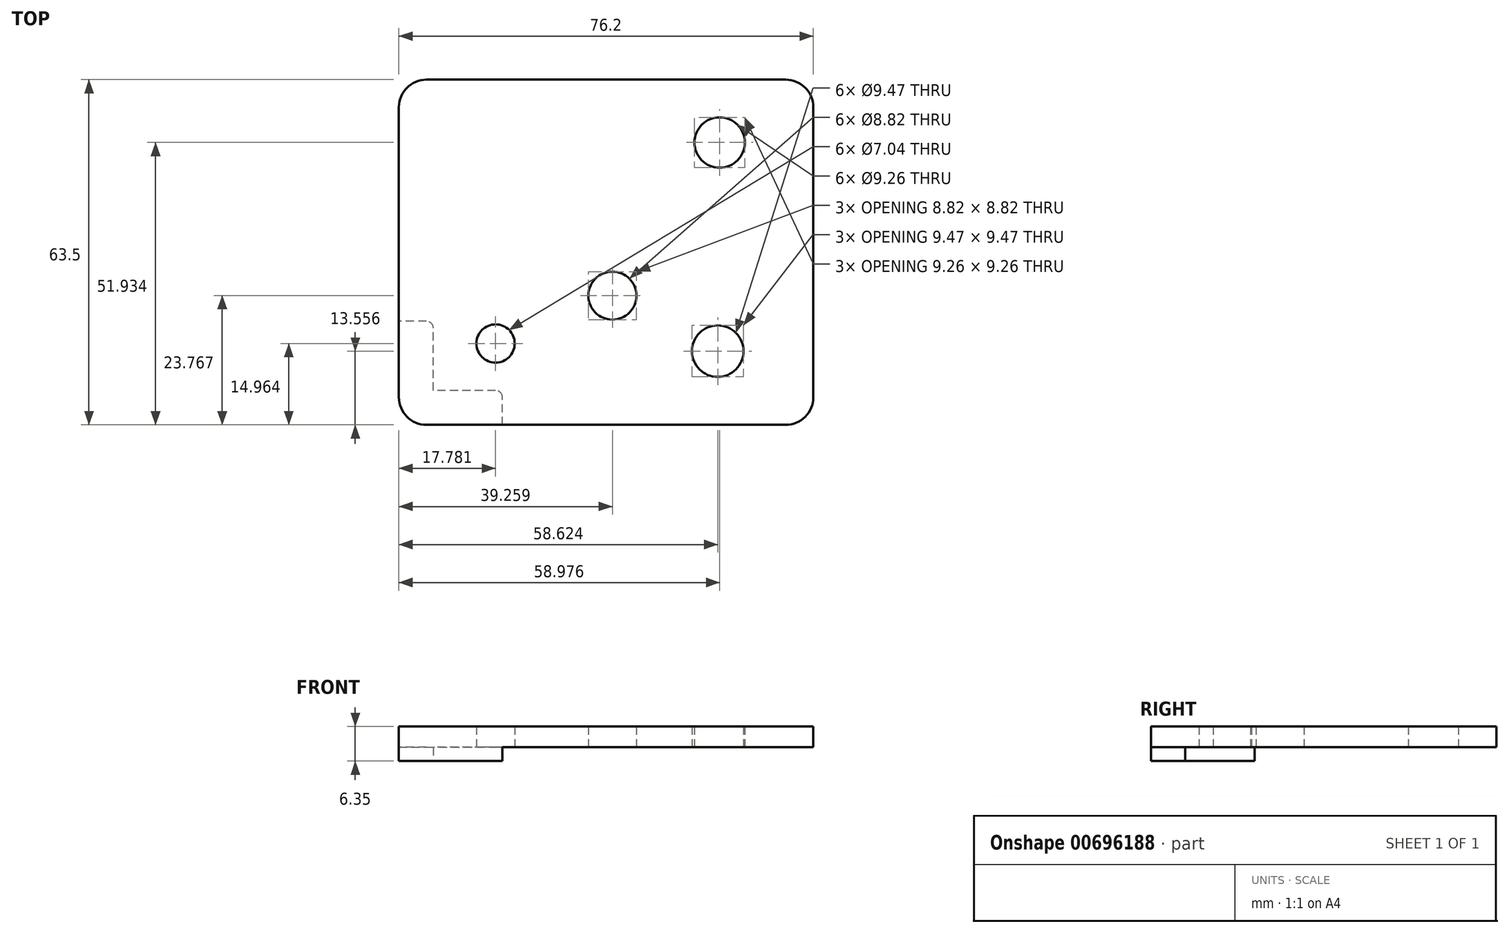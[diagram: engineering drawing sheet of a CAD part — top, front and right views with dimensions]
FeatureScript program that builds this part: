
annotation { "Feature Type Name" : "Feature", "Feature Type Description" : "" }
export const myFeature = defineFeature(function(context is Context, id is Id, definition is map)
    precondition{}
    {
        {
            var Q0;
            Q0=qCreatedBy(makeId("Top.planeOp"),FACE);
            var sketch = newSketch(context, id + "F0", { "sketchPlane" : qUnion([Q0])});
            skLineSegment(sketch, "E0.bottom", {"start": v(0, 0) * mm, "end": v(76.2, 0) * mm});
            skLineSegment(sketch, "E0.top", {"start": v(0, 63.5) * mm, "end": v(76.2, 63.5) * mm});
            skLineSegment(sketch, "E0.left", {"start": v(0, 0) * mm, "end": v(0, 63.5) * mm});
            skLineSegment(sketch, "E0.right", {"start": v(76.2, 0) * mm, "end": v(76.2, 63.5) * mm});
            skCircle(sketch, "E1", {"center": v(17.78, 14.96) * mm, "radius": 3.52 * mm});
            skCircle(sketch, "E2", {"center": v(39.26, 23.77) * mm, "radius": 4.41 * mm});
            skCircle(sketch, "E3", {"center": v(58.62, 13.56) * mm, "radius": 4.74 * mm});
            skCircle(sketch, "E4", {"center": v(58.98, 51.93) * mm, "radius": 4.63 * mm});
            skSolve(sketch);
        }
        {
            var Q0;
            Q0 = qSketchRegion(id + "F0", true);
            extrude(context, id + "F1", {"entities" : qUnion([Q0]), "depth" : 6.35 * mm, "offsetDistance" : 25.4 * mm});
        }
        {
            var Q0;
            Q0=makeQuery(id+"F1.opExtrude","CAP_FACE",FACE,{"disambiguationData":[OSD([sQuery(id+"F0.wireOp",EDGE,"E0.bottom"),sQuery(id+"F0.wireOp",EDGE,"E0.top"),sQuery(id+"F0.wireOp",EDGE,"E0.left"),sQuery(id+"F0.wireOp",EDGE,"E0.right"),sQuery(id+"F0.wireOp",EDGE,"E1"),sQuery(id+"F0.wireOp",EDGE,"E2"),sQuery(id+"F0.wireOp",EDGE,"E3"),sQuery(id+"F0.wireOp",EDGE,"E4")])],"isStart":true});
            var sketch = newSketch(context, id + "F2", { "sketchPlane" : qUnion([Q0])});
            skLineSegment(sketch, "E5", {"start": v(6.35, -6.32) * mm, "end": v(6.35, -19.05) * mm});
            skLineSegment(sketch, "E6", {"start": v(6.35, -19.05) * mm, "end": v(0, -19.05) * mm});
            skLineSegment(sketch, "E7", {"start": v(19.05, 0) * mm, "end": v(19.05, -6.32) * mm});
            skLineSegment(sketch, "E8", {"start": v(19.05, -6.32) * mm, "end": v(6.35, -6.32) * mm});
            skLineSegment(sketch, "E9", {"start": v(19.05, 0) * mm, "end": v(76.2, 0) * mm});
            skLineSegment(sketch, "E10", {"start": v(76.2, 0) * mm, "end": v(76.2, -63.5) * mm});
            skLineSegment(sketch, "E11", {"start": v(76.2, -63.5) * mm, "end": v(0, -63.5) * mm});
            skLineSegment(sketch, "E12", {"start": v(0, -63.5) * mm, "end": v(0, -19.05) * mm});
            skSolve(sketch);
        }
        {
            var Q0;
            Q0 = qSketchRegion(id + "F2", true);
            extrude(context, id + "F3", {"entities" : qUnion([Q0]), "operationType" : NewBodyOperationType.REMOVE, "oppositeDirection" : true, "depth" : 2.54 * mm, "offsetDistance" : 25.4 * mm});
        }
        {
            var Q0;
            Q0=makeQuery(id+"F1.opExtrude","SWEPT_EDGE",EDGE,{"disambiguationData":[OSD([sQuery(id+"F0.wireOp",EDGE,"E0.top"),sQuery(id+"F0.wireOp",EDGE,"E0.left")])]});
            var Q1;
            Q1=makeQuery(id+"F1.opExtrude","SWEPT_EDGE",EDGE,{"disambiguationData":[OSD([sQuery(id+"F0.wireOp",EDGE,"E0.top"),sQuery(id+"F0.wireOp",EDGE,"E0.right")])]});
            var Q2;
            Q2=makeQuery(id+"F1.opExtrude","SWEPT_EDGE",EDGE,{"disambiguationData":[OSD([sQuery(id+"F0.wireOp",EDGE,"E0.bottom"),sQuery(id+"F0.wireOp",EDGE,"E0.right")])]});
            var Q3;
            Q3=makeQuery(id+"F1.opExtrude","SWEPT_EDGE",EDGE,{"disambiguationData":[OSD([sQuery(id+"F0.wireOp",EDGE,"E0.bottom"),sQuery(id+"F0.wireOp",EDGE,"E0.left")])]});
            fillet(context, id + "F4", {"entities" : qUnion([Q0, Q1, Q2, Q3]), "radius" : 5.08 * mm, "tangentPropagation" : true, "allowEdgeOverflow" : false});
        }
        {
            var Q0;
            Q0=makeQuery(id+"F3.boolean.opBoolean","COPY",EDGE,{"derivedFrom":makeQuery(id+"F3.opExtrude","SWEPT_EDGE",EDGE,{"disambiguationData":[OSD([sQuery(id+"F2.wireOp",EDGE,"E5"),sQuery(id+"F2.wireOp",EDGE,"E6")])]})});
            var Q1;
            Q1=makeQuery(id+"F3.boolean.opBoolean","COPY",EDGE,{"derivedFrom":makeQuery(id+"F3.opExtrude","SWEPT_EDGE",EDGE,{"disambiguationData":[OSD([sQuery(id+"F2.wireOp",EDGE,"E7"),sQuery(id+"F2.wireOp",EDGE,"E8")])]})});
            var Q2;
            Q2=makeQuery(id+"F3.boolean.opBoolean","COPY",EDGE,{"derivedFrom":makeQuery(id+"F3.opExtrude","SWEPT_EDGE",EDGE,{"disambiguationData":[OSD([sQuery(id+"F0.wireOp",EDGE,"E0.left"),sQuery(id+"F2.wireOp",EDGE,"E6"),sQuery(id+"F2.wireOp",EDGE,"E12")])]})});
            var Q3;
            Q3=makeQuery(id+"F3.boolean.opBoolean","COPY",EDGE,{"derivedFrom":makeQuery(id+"F3.opExtrude","SWEPT_EDGE",EDGE,{"disambiguationData":[OSD([sQuery(id+"F0.wireOp",EDGE,"E0.bottom"),sQuery(id+"F2.wireOp",EDGE,"E7"),sQuery(id+"F2.wireOp",EDGE,"E9")])]})});
            fillet(context, id + "F5", {"entities" : qUnion([Q0, Q1, Q2, Q3]), "radius" : 1.27 * mm, "tangentPropagation" : true, "allowEdgeOverflow" : false});
        }
    });
